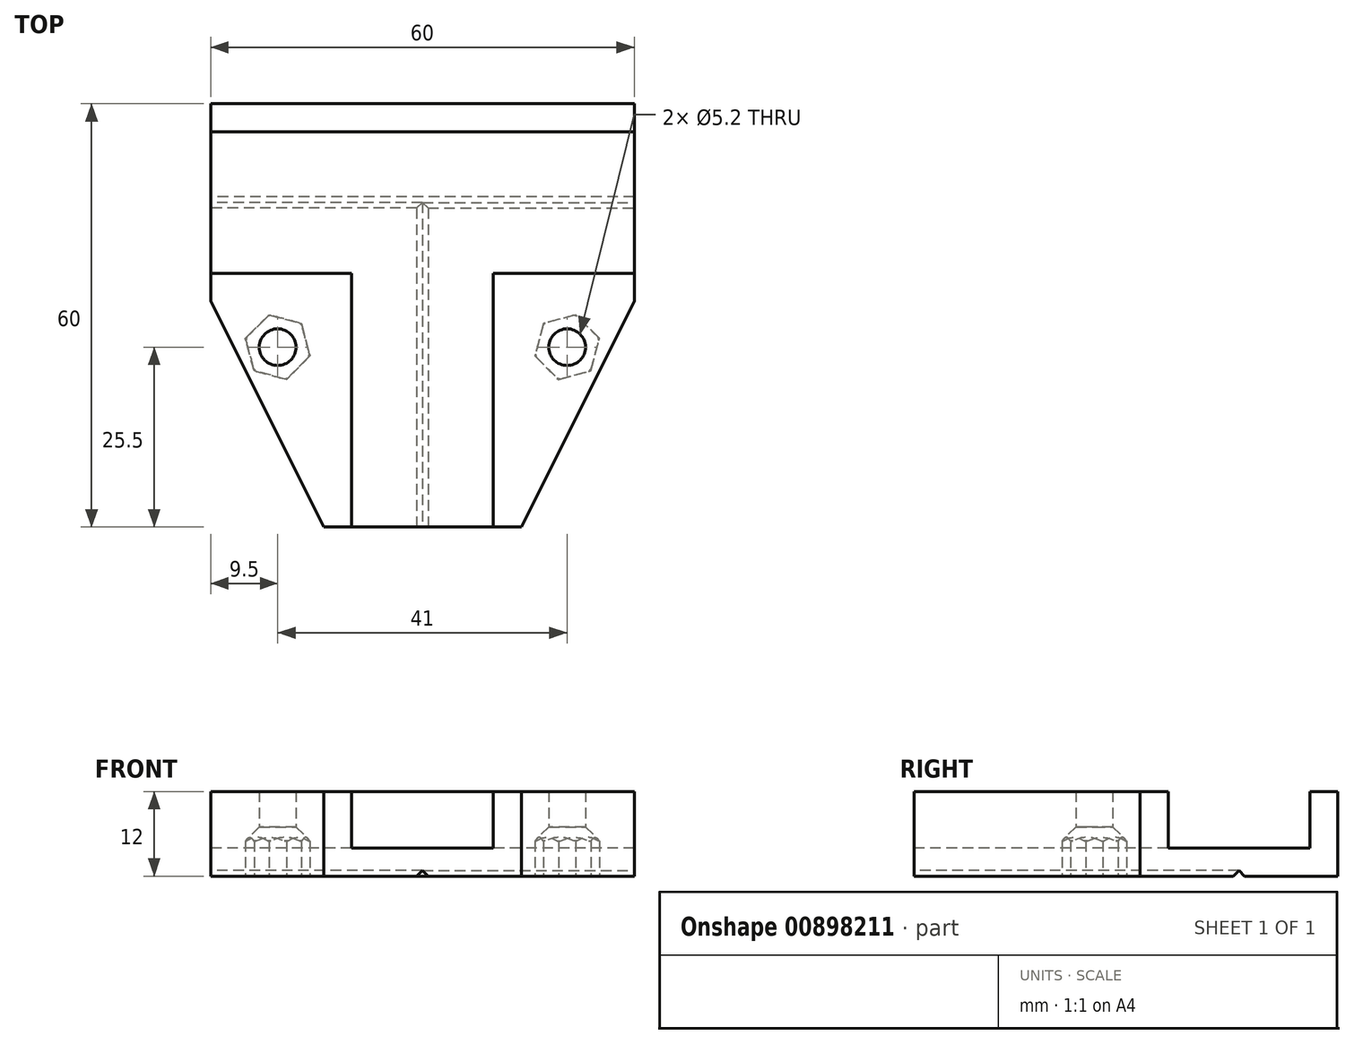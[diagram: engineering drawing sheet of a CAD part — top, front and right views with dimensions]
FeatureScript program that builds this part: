
annotation { "Feature Type Name" : "Feature", "Feature Type Description" : "" }
export const myFeature = defineFeature(function(context is Context, id is Id, definition is map)
    precondition{}
    {
        {
            var Q0;
            Q0=qCreatedBy(makeId("Top.planeOp"),FACE);
            var sketch = newSketch(context, id + "F0", { "sketchPlane" : qUnion([Q0])});
            skLineSegment(sketch, "E0", {"start": v(0, 14) * mm, "end": v(-30, 14) * mm});
            skLineSegment(sketch, "E1", {"start": v(-30, 14) * mm, "end": v(-30, -14) * mm});
            skLineSegment(sketch, "E2", {"start": v(-30, -14) * mm, "end": v(-14, -46) * mm});
            skLineSegment(sketch, "E3", {"start": v(-14, -46) * mm, "end": v(0, -46) * mm});
            skLineSegment(sketch, "E4", {"start": v(0, -46) * mm, "end": v(0, 14) * mm});
            skLineSegment(sketch, "E5", {"start": v(0, 0) * mm, "end": v(-30, 0) * mm, "construction": true});
            skCircle(sketch, "E6", {"center": v(-20.5, -20.5) * mm, "radius": 6.5 * mm, "construction": true});
            skLineSegment(sketch, "E7", {"start": v(-30, -14) * mm, "end": v(0, -14) * mm, "construction": true});
            skLineSegment(sketch, "E8", {"start": v(-14, -46) * mm, "end": v(-14, -14) * mm, "construction": true});
            skCircle(sketch, "E9", {"center": v(-20.5, -20.5) * mm, "radius": 2.6 * mm});
            skSolve(sketch);
        }
        {
            var Q0;
            Q0=qSketchRegion(id+"F0",true);
            extrude(context, id + "F1", {"entities" : qUnion([Q0]), "depth" : 12 * mm, "offsetDistance" : 25 * mm});
        }
        {
            var Q0;
            Q0=makeQuery(id+"F1.opExtrude","SWEPT_FACE",FACE,{"disambiguationData":[OSD([sQuery(id+"F0.wireOp",EDGE,"E3")])]});
            var sketch = newSketch(context, id + "F2", { "sketchPlane" : qUnion([Q0])});
            skLineSegment(sketch, "E10.bottom", {"start": v(0, 12) * mm, "end": v(-10.05, 12) * mm});
            skLineSegment(sketch, "E10.top", {"start": v(0, 4) * mm, "end": v(-10.05, 4) * mm});
            skLineSegment(sketch, "E10.left", {"start": v(0, 12) * mm, "end": v(0, 4) * mm});
            skLineSegment(sketch, "E10.right", {"start": v(-10.05, 12) * mm, "end": v(-10.05, 4) * mm});
            skLineSegment(sketch, "E11", {"start": v(0, 0) * mm, "end": v(0, 0.8) * mm});
            skLineSegment(sketch, "E12", {"start": v(0, 0.8) * mm, "end": v(-0.8, 0) * mm});
            skLineSegment(sketch, "E13", {"start": v(-0.8, 0) * mm, "end": v(0, 0) * mm});
            skSolve(sketch);
        }
        {
            var Q0;
            Q0=makeQuery(id+"F1.opExtrude","SWEPT_FACE",FACE,{"disambiguationData":[OSD([sQuery(id+"F0.wireOp",EDGE,"E1")])]});
            var sketch = newSketch(context, id + "F3", { "sketchPlane" : qUnion([Q0])});
            skLineSegment(sketch, "E14.bottom", {"start": v(-10.05, 12) * mm, "end": v(10.05, 12) * mm});
            skLineSegment(sketch, "E14.top", {"start": v(-10.05, 4) * mm, "end": v(10.05, 4) * mm});
            skLineSegment(sketch, "E14.left", {"start": v(-10.05, 12) * mm, "end": v(-10.05, 4) * mm});
            skLineSegment(sketch, "E14.right", {"start": v(10.05, 12) * mm, "end": v(10.05, 4) * mm});
            skPoint(sketch, "E15", {"position": v(0, 12) * mm});
            skLineSegment(sketch, "E16", {"start": v(-0.8, 0) * mm, "end": v(0.8, 0) * mm});
            skLineSegment(sketch, "E17", {"start": v(0.8, 0) * mm, "end": v(0, 0.8) * mm});
            skLineSegment(sketch, "E18", {"start": v(0, 0.8) * mm, "end": v(-0.8, 0) * mm});
            skSolve(sketch);
        }
        {
            var Q0;
            Q0=qSketchRegion(id+"F3",true);
            extrude(context, id + "F4", {"entities" : qUnion([Q0]), "operationType" : NewBodyOperationType.REMOVE, "endBound" : BoundingType.THROUGH_ALL, "oppositeDirection" : true, "depth" : 25 * mm, "offsetDistance" : 25 * mm});
        }
        {
            var Q0;
            Q0=qSketchRegion(id+"F2",true);
            extrude(context, id + "F5", {"entities" : qUnion([Q0]), "operationType" : NewBodyOperationType.REMOVE, "endBound" : BoundingType.UP_TO_NEXT, "oppositeDirection" : true, "depth" : 25 * mm, "offsetDistance" : 25 * mm});
        }
        {
            var Q0;
            Q0=makeQuery(id+"F0.imprint","IMPRINT",FACE,{"disambiguationData":[TD([[makeQuery(id+"F0.imprint","IMPRINT",EDGE,{"derivedFrom":sQuery(id+"F0.wireOp",EDGE,"E0")}),1.0]])]});
            var sketch = newSketch(context, id + "F6", { "sketchPlane" : qUnion([Q0])});
            skCircle(sketch, "E19.cCircle", {"center": v(-20.5, -20.5) * mm, "radius": 4.1 * mm, "construction": true});
            skLineSegment(sketch, "E19.0", {"start": v(-17.15, -17.15) * mm, "end": v(-15.93, -21.73) * mm});
            skLineSegment(sketch, "E19.1", {"start": v(-15.93, -21.73) * mm, "end": v(-19.27, -25.07) * mm});
            skLineSegment(sketch, "E19.2", {"start": v(-19.27, -25.07) * mm, "end": v(-23.85, -23.85) * mm});
            skLineSegment(sketch, "E19.3", {"start": v(-23.85, -23.85) * mm, "end": v(-25.07, -19.27) * mm});
            skLineSegment(sketch, "E19.4", {"start": v(-25.07, -19.27) * mm, "end": v(-21.73, -15.93) * mm});
            skLineSegment(sketch, "E19.5", {"start": v(-21.73, -15.93) * mm, "end": v(-17.15, -17.15) * mm});
            skPoint(sketch, "E19.0.midPoint", {"position": v(-16.54, -19.44) * mm});
            skLineSegment(sketch, "E20", {"start": v(-20.5, -20.5) * mm, "end": v(-14, -14) * mm, "construction": true});
            skSolve(sketch);
        }
        {
            var Q0;
            Q0=qSketchRegion(id+"F6",true);
            extrude(context, id + "F7", {"entities" : qUnion([Q0]), "operationType" : NewBodyOperationType.REMOVE, "depth" : 5 * mm, "offsetDistance" : 25 * mm});
        }
        {
            var Q0;
            Q0=makeQuery(id+"F1.opExtrude","SWEPT_BODY",BODY,{"disambiguationData":[OSD([sQuery(id+"F0.wireOp",EDGE,"E0"),sQuery(id+"F0.wireOp",EDGE,"E1"),sQuery(id+"F0.wireOp",EDGE,"E2"),sQuery(id+"F0.wireOp",EDGE,"E3"),sQuery(id+"F0.wireOp",EDGE,"E4"),sQuery(id+"F0.wireOp",EDGE,"E9")])]});
            var Q1;
            Q1=qCreatedBy(makeId("Right.planeOp"),FACE);
            mirror(context, id + "F8", {"operationType" : NewBodyOperationType.ADD, "entities" : qUnion([Q0]), "mirrorPlane" : qUnion([Q1])});
        }
        {
            var Q0;
            Q0=makeQuery(id+"F8.opPattern","COPY",EDGE,{"derivedFrom":makeQuery(id+"F7.boolean.opBoolean","INTERSECT",EDGE,{"derivedFrom":[makeQuery(id+"F1.opExtrude","SWEPT_FACE",FACE,{"disambiguationData":[OSD([sQuery(id+"F0.wireOp",EDGE,"E9")])]}),makeQuery(id+"F7.opExtrude","CAP_FACE",FACE,{"disambiguationData":[OSD([sQuery(id+"F6.wireOp",EDGE,"E19.0"),sQuery(id+"F6.wireOp",EDGE,"E19.1"),sQuery(id+"F6.wireOp",EDGE,"E19.2"),sQuery(id+"F6.wireOp",EDGE,"E19.3"),sQuery(id+"F6.wireOp",EDGE,"E19.4"),sQuery(id+"F6.wireOp",EDGE,"E19.5")])],"isStart":false})]}),"instanceName":"1"});
            var Q1;
            Q1=makeQuery(id+"F7.boolean.opBoolean","INTERSECT",EDGE,{"derivedFrom":[makeQuery(id+"F1.opExtrude","SWEPT_FACE",FACE,{"disambiguationData":[OSD([sQuery(id+"F0.wireOp",EDGE,"E9")])]}),makeQuery(id+"F7.opExtrude","CAP_FACE",FACE,{"disambiguationData":[OSD([sQuery(id+"F6.wireOp",EDGE,"E19.0"),sQuery(id+"F6.wireOp",EDGE,"E19.1"),sQuery(id+"F6.wireOp",EDGE,"E19.2"),sQuery(id+"F6.wireOp",EDGE,"E19.3"),sQuery(id+"F6.wireOp",EDGE,"E19.4"),sQuery(id+"F6.wireOp",EDGE,"E19.5")])],"isStart":false})]});
            chamfer(context, id + "F9", {"entities" : qUnion([Q0, Q1]), "width" : 2 * mm, "tangentPropagation" : true});
        }
    });
